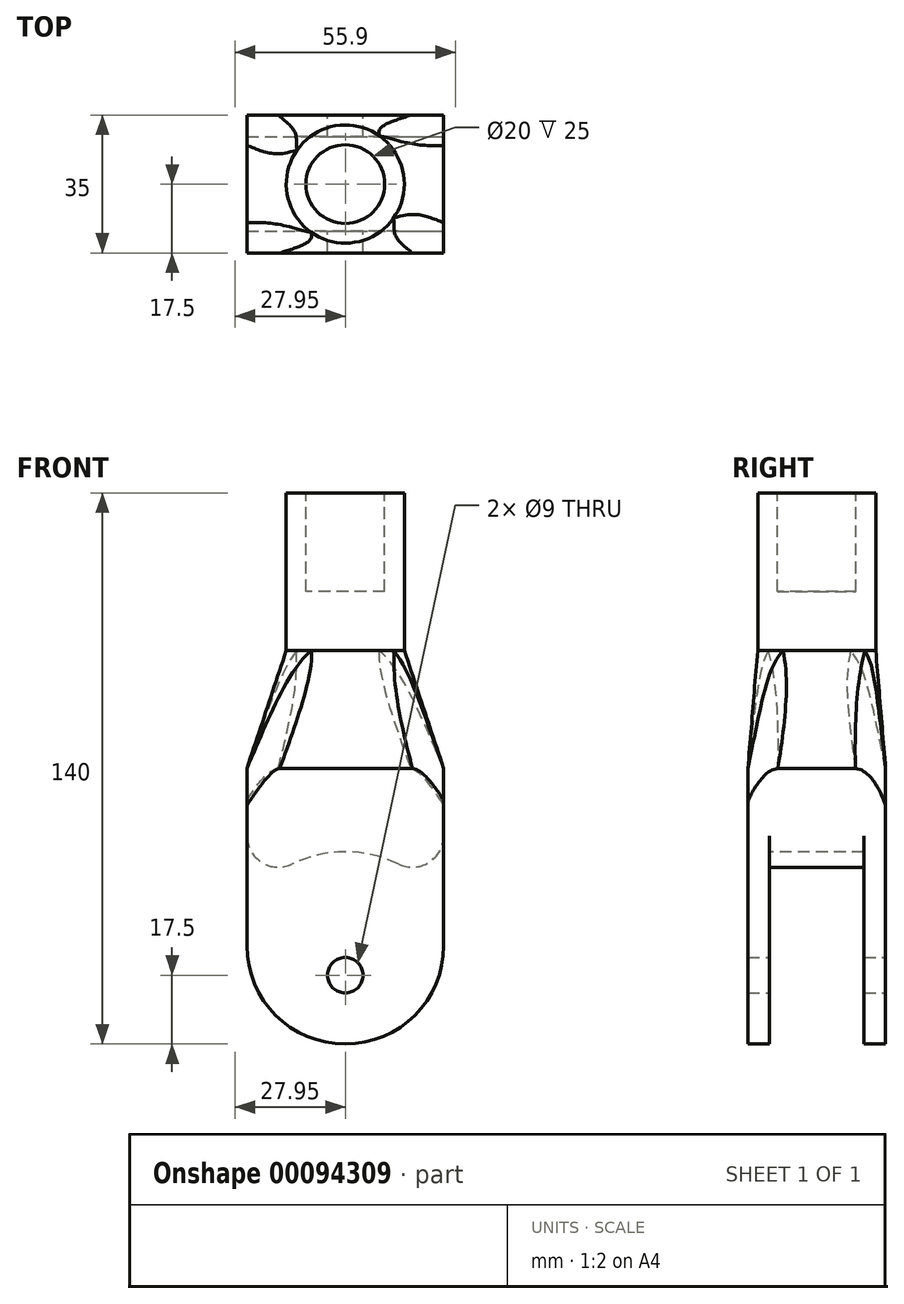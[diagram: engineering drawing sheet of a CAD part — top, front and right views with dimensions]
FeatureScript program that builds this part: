
annotation { "Feature Type Name" : "Feature", "Feature Type Description" : "" }
export const myFeature = defineFeature(function(context is Context, id is Id, definition is map)
    precondition{}
    {
        {
            var Q0;
            Q0=qCreatedBy(makeId("Front.planeOp"),FACE);
            var sketch = newSketch(context, id + "F0", { "sketchPlane" : qUnion([Q0])});
            skLineSegment(sketch, "E0.bottom", {"start": v(-25, 35) * mm, "end": v(25, 35) * mm});
            skLineSegment(sketch, "E0.top", {"start": v(-25, -35) * mm, "end": v(25, -35) * mm});
            skLineSegment(sketch, "E0.left", {"start": v(-25, 35) * mm, "end": v(-25, -35) * mm});
            skLineSegment(sketch, "E0.right", {"start": v(25, 35) * mm, "end": v(25, -35) * mm});
            skPoint(sketch, "E0.middle", {"position": v(0, 0) * mm});
            skLineSegment(sketch, "E1", {"start": v(0, 0) * mm, "end": v(0, -35) * mm, "construction": true});
            skCircle(sketch, "E2", {"center": v(0, -17.5) * mm, "radius": 4.5 * mm});
            skSolve(sketch);
        }
        {
            var Q0;
            Q0=makeQuery(id+"F0.imprint","IMPRINT",FACE,{"disambiguationData":[TD([[makeQuery(id+"F0.imprint","IMPRINT",EDGE,{"derivedFrom":sQuery(id+"F0.wireOp",EDGE,"E0.bottom")}),-1.0]])]});
            extrude(context, id + "F1", {"entities" : qUnion([Q0]), "endBound" : BoundingType.SYMMETRIC, "depth" : 35 * mm});
        }
        {
            var Q0;
            Q0=qCreatedBy(makeId("Front.planeOp"),FACE);
            var sketch = newSketch(context, id + "F2", { "sketchPlane" : qUnion([Q0])});
            skLineSegment(sketch, "E3.bottom", {"start": v(27.26, -35.76) * mm, "end": v(-27.26, -35.76) * mm});
            skLineSegment(sketch, "E3.top", {"start": v(27.26, 1.15) * mm, "end": v(-27.26, 1.15) * mm});
            skLineSegment(sketch, "E3.left", {"start": v(27.26, -35.76) * mm, "end": v(27.26, 1.15) * mm});
            skLineSegment(sketch, "E3.right", {"start": v(-27.26, -35.76) * mm, "end": v(-27.26, 1.15) * mm});
            skPoint(sketch, "E3.middle", {"position": v(0, -17.3) * mm});
            skSolve(sketch);
        }
        {
            var Q0;
            Q0 = qSketchRegion(id + "F2", true);
            extrude(context, id + "F3", {"entities" : qUnion([Q0]), "operationType" : NewBodyOperationType.REMOVE, "oppositeDirection" : true, "depth" : 12 * mm, "hasSecondDirection" : true, "secondDirectionOppositeDirection" : false, "secondDirectionDepth" : 12 * mm});
        }
        {
            var Q0;
            Q0=qCreatedBy(makeId("Front.planeOp"),FACE);
            var sketch = newSketch(context, id + "F4", { "sketchPlane" : qUnion([Q0])});
            skCircle(sketch, "E4", {"center": v(0, -17.31) * mm, "radius": 31.14 * mm});
            skSolve(sketch);
        }
        {
            var Q0;
            Q0=makeQuery(id+"F4.imprint","IMPRINT",FACE,{"disambiguationData":[TD([[makeQuery(id+"F4.imprint","IMPRINT",EDGE,{"derivedFrom":sQuery(id+"F4.wireOp",EDGE,"E4")}),1.0]])]});
            extrude(context, id + "F5", {"entities" : qUnion([Q0]), "operationType" : NewBodyOperationType.REMOVE, "oppositeDirection" : true, "depth" : 12 * mm, "hasSecondDirection" : true, "secondDirectionOppositeDirection" : false, "secondDirectionDepth" : 12 * mm});
        }
        {
            var Q0;
            {var subQ0=sQuery(id+"F0.wireOp",EDGE,"E0.left");var subQ1=sQuery(id+"F0.wireOp",EDGE,"E0.top");Q0=makeQuery(id+"F3.boolean.opBoolean","SPLIT",EDGE,{"disambiguationData":[TD([makeQuery(id+"F3.opExtrude","CAP_FACE",FACE,{"disambiguationData":[OSD([sQuery(id+"F2.wireOp",EDGE,"E3.bottom"),sQuery(id+"F2.wireOp",EDGE,"E3.top"),sQuery(id+"F2.wireOp",EDGE,"E3.left"),sQuery(id+"F2.wireOp",EDGE,"E3.right")])],"isStart":true})])],"derivedFrom":makeQuery(id+"F1.opExtrude","SWEPT_EDGE",EDGE,{"disambiguationData":[OSD([subQ1,subQ0])]})});}
            var Q1;
            {var subQ0=sQuery(id+"F0.wireOp",EDGE,"E0.left");var subQ1=sQuery(id+"F0.wireOp",EDGE,"E0.top");Q1=makeQuery(id+"F3.boolean.opBoolean","SPLIT",EDGE,{"disambiguationData":[TD([makeQuery(id+"F3.opExtrude","CAP_FACE",FACE,{"disambiguationData":[OSD([sQuery(id+"F2.wireOp",EDGE,"E3.bottom"),sQuery(id+"F2.wireOp",EDGE,"E3.top"),sQuery(id+"F2.wireOp",EDGE,"E3.left"),sQuery(id+"F2.wireOp",EDGE,"E3.right")])],"isStart":false})])],"derivedFrom":makeQuery(id+"F1.opExtrude","SWEPT_EDGE",EDGE,{"disambiguationData":[OSD([subQ1,subQ0])]})});}
            var Q2;
            {var subQ0=sQuery(id+"F0.wireOp",EDGE,"E0.right");var subQ1=sQuery(id+"F0.wireOp",EDGE,"E0.top");Q2=makeQuery(id+"F3.boolean.opBoolean","SPLIT",EDGE,{"disambiguationData":[TD([makeQuery(id+"F3.opExtrude","CAP_FACE",FACE,{"disambiguationData":[OSD([sQuery(id+"F2.wireOp",EDGE,"E3.bottom"),sQuery(id+"F2.wireOp",EDGE,"E3.top"),sQuery(id+"F2.wireOp",EDGE,"E3.left"),sQuery(id+"F2.wireOp",EDGE,"E3.right")])],"isStart":false})])],"derivedFrom":makeQuery(id+"F1.opExtrude","SWEPT_EDGE",EDGE,{"disambiguationData":[OSD([subQ1,subQ0])]})});}
            var Q3;
            {var subQ0=sQuery(id+"F0.wireOp",EDGE,"E0.right");var subQ1=sQuery(id+"F0.wireOp",EDGE,"E0.top");Q3=makeQuery(id+"F3.boolean.opBoolean","SPLIT",EDGE,{"disambiguationData":[TD([makeQuery(id+"F3.opExtrude","CAP_FACE",FACE,{"disambiguationData":[OSD([sQuery(id+"F2.wireOp",EDGE,"E3.bottom"),sQuery(id+"F2.wireOp",EDGE,"E3.top"),sQuery(id+"F2.wireOp",EDGE,"E3.left"),sQuery(id+"F2.wireOp",EDGE,"E3.right")])],"isStart":true})])],"derivedFrom":makeQuery(id+"F1.opExtrude","SWEPT_EDGE",EDGE,{"disambiguationData":[OSD([subQ1,subQ0])]})});}
            fillet(context, id + "F6", {"entities" : qUnion([Q0, Q1, Q2, Q3]), "radius" : 25 * mm, "tangentPropagation" : true, "allowEdgeOverflow" : false});
        }
        {
            var Q0;
            Q0=makeQuery(id+"F5.boolean.opBoolean","INTERSECT",EDGE,{"derivedFrom":[makeQuery(id+"F1.opExtrude","SWEPT_FACE",FACE,{"disambiguationData":[OSD([sQuery(id+"F0.wireOp",EDGE,"E0.left")])]}),makeQuery(id+"F5.opExtrude","SWEPT_FACE",FACE,{"disambiguationData":[OSD([sQuery(id+"F4.wireOp",EDGE,"E4")])]})]});
            var Q1;
            Q1=makeQuery(id+"F5.boolean.opBoolean","INTERSECT",EDGE,{"derivedFrom":[makeQuery(id+"F1.opExtrude","SWEPT_FACE",FACE,{"disambiguationData":[OSD([sQuery(id+"F0.wireOp",EDGE,"E0.right")])]}),makeQuery(id+"F5.opExtrude","SWEPT_FACE",FACE,{"disambiguationData":[OSD([sQuery(id+"F4.wireOp",EDGE,"E4")])]})]});
            fillet(context, id + "F7", {"entities" : qUnion([Q0, Q1]), "radius" : 8 * mm, "tangentPropagation" : true, "allowEdgeOverflow" : false});
        }
        {
            var Q0;
            Q0=makeQuery(id+"F1.opExtrude","SWEPT_FACE",FACE,{"disambiguationData":[OSD([sQuery(id+"F0.wireOp",EDGE,"E0.bottom")])]});
            cPlane(context, id + "F8", {"entities" : qUnion([Q0]), "cplaneType" : CPlaneType.OFFSET, "offset" : 30 * mm, "width" : 150 * mm, "height" : 150 * mm});
        }
        {
            var Q0;
            Q0=qCreatedBy(id+"F8.planeOp",FACE);
            var sketch = newSketch(context, id + "F9", { "sketchPlane" : qUnion([Q0])});
            skCircle(sketch, "E5", {"center": v(0, 0) * mm, "radius": 15 * mm});
            skSolve(sketch);
        }
        {
            var Q0;
            Q0 = qSketchRegion(id + "F9", true);
            extrude(context, id + "F10", {"entities" : qUnion([Q0]), "depth" : 40 * mm});
        }
        {
            var Q1;
            Q1=makeQuery(id+"F1.opExtrude","SWEPT_FACE",FACE,{"disambiguationData":[OSD([sQuery(id+"F0.wireOp",EDGE,"E0.bottom")])]});
            var Q2;
            Q2=makeQuery(id+"F10.opExtrude","CAP_FACE",FACE,{"disambiguationData":[OSD([sQuery(id+"F9.wireOp",EDGE,"E5")])],"isStart":true});
            loft(context, id + "F11", {"operationType" : NewBodyOperationType.ADD, "sheetProfilesArray" : [{ "sheetProfileEntities" : qUnion([Q1]) }, { "sheetProfileEntities" : qUnion([Q2]) }]});
        }
        {
            var Q0;
            Q0=makeQuery(id+"F11.opLoft","SWEPT_EDGE",EDGE,{"disambiguationData":[OSD([sQuery(id+"F0.wireOp",EDGE,"E0.bottom"),sQuery(id+"F0.wireOp",EDGE,"E0.left"),sQuery(id+"F0.wireOp",EDGE,"E0.right"),sQuery(id+"F9.wireOp",EDGE,"E5")])]});
            var Q1;
            Q1=makeQuery(id+"F11.opLoft","SWEPT_EDGE",EDGE,{"disambiguationData":[OSD([sQuery(id+"F0.wireOp",EDGE,"E0.bottom"),sQuery(id+"F0.wireOp",EDGE,"E0.right"),sQuery(id+"F9.wireOp",EDGE,"E5")])]});
            var Q2;
            Q2=makeQuery(id+"F11.opLoft","SWEPT_EDGE",EDGE,{"disambiguationData":[OSD([sQuery(id+"F0.wireOp",EDGE,"E0.bottom"),sQuery(id+"F0.wireOp",EDGE,"E0.left"),sQuery(id+"F9.wireOp",EDGE,"E5")])]});
            var Q3;
            Q3=makeQuery(id+"F11.opLoft","SWEPT_EDGE",EDGE,{"disambiguationData":[OSD([sQuery(id+"F0.wireOp",EDGE,"E0.bottom"),sQuery(id+"F0.wireOp",EDGE,"E0.left")])]});
            fillet(context, id + "F12", {"entities" : qUnion([Q0, Q1, Q2, Q3]), "radius" : 8 * mm, "tangentPropagation" : true, "allowEdgeOverflow" : false});
        }
        {
            var Q0;
            Q0=makeQuery(id+"F10.opExtrude","CAP_FACE",FACE,{"disambiguationData":[OSD([sQuery(id+"F9.wireOp",EDGE,"E5")])],"isStart":false});
            var sketch = newSketch(context, id + "F13", { "sketchPlane" : qUnion([Q0])});
            skCircle(sketch, "E6", {"center": v(0, 0) * mm, "radius": 10 * mm});
            skSolve(sketch);
        }
        {
            var Q0;
            Q0 = qSketchRegion(id + "F13", true);
            extrude(context, id + "F14", {"entities" : qUnion([Q0]), "operationType" : NewBodyOperationType.REMOVE, "oppositeDirection" : true, "depth" : 25 * mm});
        }
    });
